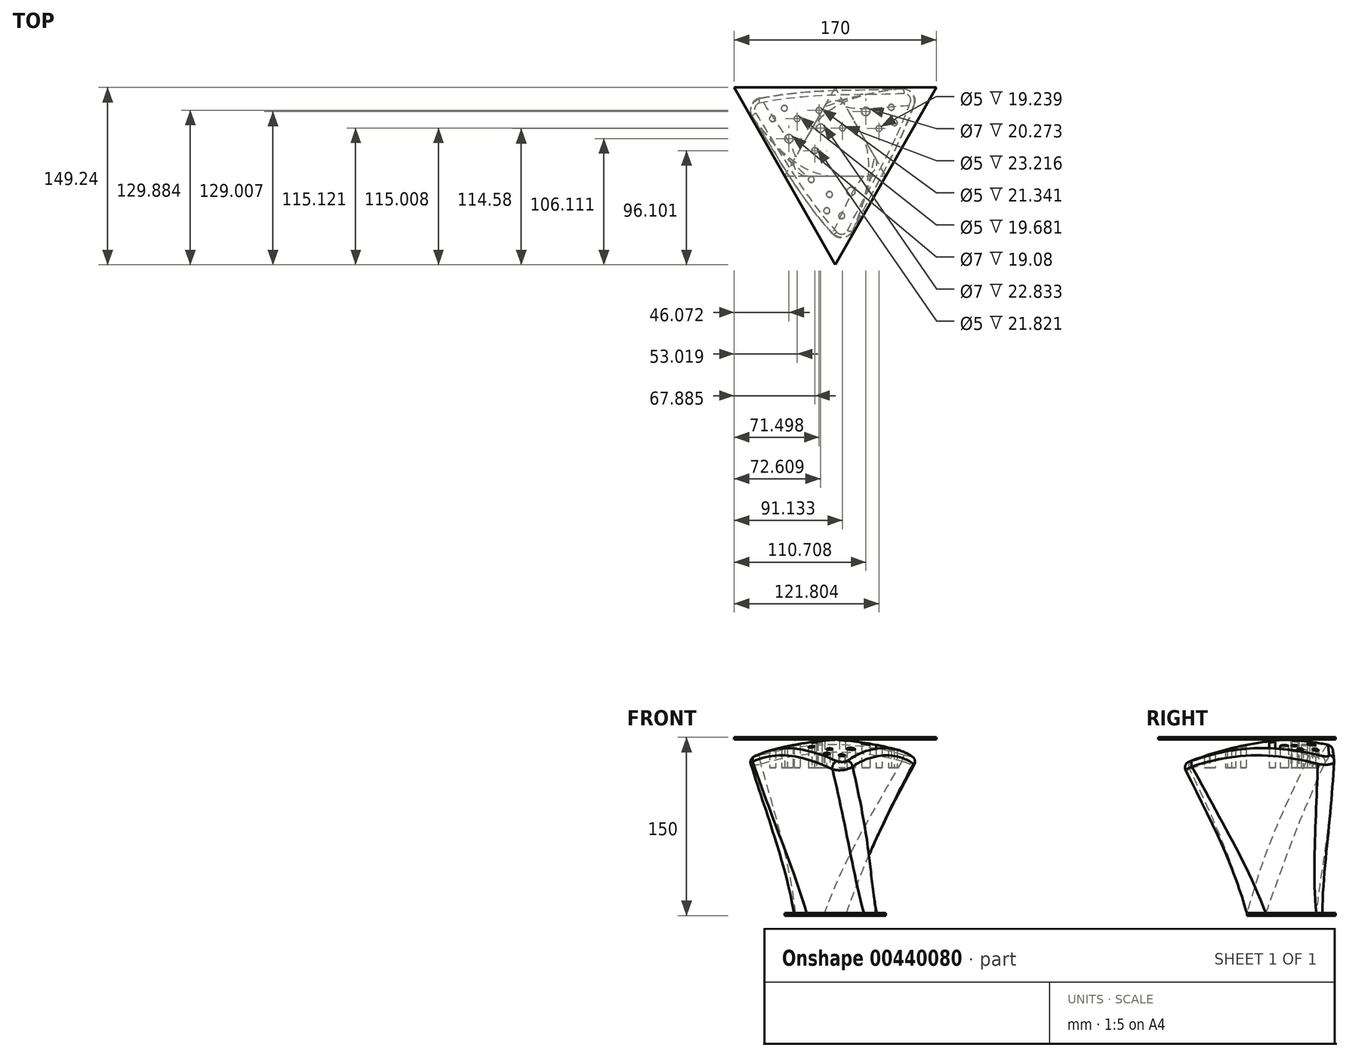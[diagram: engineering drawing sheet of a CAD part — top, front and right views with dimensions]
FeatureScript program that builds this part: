
annotation { "Feature Type Name" : "Feature", "Feature Type Description" : "" }
export const myFeature = defineFeature(function(context is Context, id is Id, definition is map)
    precondition{}
    {
        {
            var Q0;
            Q0=qCreatedBy(makeId("Top.planeOp"),FACE);
            var sketch = newSketch(context, id + "F0", { "sketchPlane" : qUnion([Q0])});
            skLineSegment(sketch, "E0", {"start": v(-85, 50.34) * mm, "end": v(85, 50.34) * mm});
            skLineSegment(sketch, "E1", {"start": v(85, 50.34) * mm, "end": v(0, -98.9) * mm});
            skPoint(sketch, "E1.endSnap0", {"position": v(0, 50.34) * mm});
            skLineSegment(sketch, "E2", {"start": v(0, -98.9) * mm, "end": v(-85, 50.34) * mm});
            skLineSegment(sketch, "E3", {"start": v(0, 50.34) * mm, "end": v(-42.5, -24.28) * mm});
            skLineSegment(sketch, "E4", {"start": v(-42.5, -24.28) * mm, "end": v(42.5, -24.28) * mm});
            skLineSegment(sketch, "E5", {"start": v(42.5, -24.28) * mm, "end": v(0, 50.34) * mm});
            skPoint(sketch, "E6.endSnap0", {"position": v(21.25, 13.03) * mm});
            skSolve(sketch);
        }
        {
            var Q0;
            Q0=makeQuery(id+"F0.imprint","IMPRINT",FACE,{"disambiguationData":[TD([[makeQuery(id+"F0.imprint","IMPRINT",EDGE,{"derivedFrom":sQuery(id+"F0.wireOp",EDGE,"E3")}),1.0]])]});
            extrude(context, id + "F1", {"entities" : qUnion([Q0]), "depth" : 2 * mm});
        }
        {
            var Q0;
            {var subQ3=sQuery(id+"F0.wireOp",EDGE,"E3");Q0=makeQuery(id+"F0.imprint","IMPRINT",FACE,{"disambiguationData":[TD([[makeQuery(id+"F0.imprint","IMPRINT",EDGE,{"derivedFrom":subQ3}),-1.0]])]});}
            var Q1;
            {var subQ3=sQuery(id+"F0.wireOp",EDGE,"E4");Q1=makeQuery(id+"F0.imprint","IMPRINT",FACE,{"disambiguationData":[TD([[makeQuery(id+"F0.imprint","IMPRINT",EDGE,{"derivedFrom":subQ3}),-1.0]])]});}
            var Q2;
            Q2=makeQuery(id+"F0.imprint","IMPRINT",FACE,{"disambiguationData":[TD([[makeQuery(id+"F0.imprint","IMPRINT",EDGE,{"derivedFrom":sQuery(id+"F0.wireOp",EDGE,"E3")}),1.0]])]});
            var Q3;
            {var subQ3=sQuery(id+"F0.wireOp",EDGE,"E5");Q3=makeQuery(id+"F0.imprint","IMPRINT",FACE,{"disambiguationData":[TD([[makeQuery(id+"F0.imprint","IMPRINT",EDGE,{"derivedFrom":subQ3}),-1.0]])]});}
            extrude(context, id + "F2", {"entities" : qUnion([Q0, Q1, Q2, Q3]), "depth" : 2 * mm});
        }
        {
            var Q0;
            Q0=makeQuery(id+"F2.opExtrude","SWEPT_BODY",BODY,{"disambiguationData":[OSD([sQuery(id+"F0.wireOp",EDGE,"E0"),sQuery(id+"F0.wireOp",EDGE,"E1"),sQuery(id+"F0.wireOp",EDGE,"E2")])]});
            transform(context, id + "F3", {"entities" : qUnion([Q0]), "transformType" : TransformType.TRANSLATION_3D, "dx" : 0 * mm, "dy" : 0 * mm, "dz" : 148 * mm, "makeCopy" : false});
        }
        {
            var Q2;
            Q2=makeQuery(id+"F2.opExtrude","CAP_FACE",FACE,{"disambiguationData":[OSD([sQuery(id+"F0.wireOp",EDGE,"E0"),sQuery(id+"F0.wireOp",EDGE,"E1"),sQuery(id+"F0.wireOp",EDGE,"E2")])],"isStart":true});
            var Q3;
            Q3=makeQuery(id+"F1.opExtrude","CAP_FACE",FACE,{"disambiguationData":[OSD([sQuery(id+"F0.wireOp",EDGE,"E3"),sQuery(id+"F0.wireOp",EDGE,"E4"),sQuery(id+"F0.wireOp",EDGE,"E5")])],"isStart":false});
            loft(context, id + "F4", {"sheetProfilesArray" : [{ "sheetProfileEntities" : qUnion([Q2]) }, { "sheetProfileEntities" : qUnion([Q3]) }]});
        }
        {
            var Q0;
            Q0=makeQuery(id+"F4.opLoft","SWEPT_EDGE",EDGE,{"disambiguationData":[OSD([sQuery(id+"F0.wireOp",EDGE,"E0"),sQuery(id+"F0.wireOp",EDGE,"E1"),sQuery(id+"F0.wireOp",EDGE,"E3"),sQuery(id+"F0.wireOp",EDGE,"E5")])]});
            var Q1;
            Q1=makeQuery(id+"F4.opLoft","SWEPT_EDGE",EDGE,{"disambiguationData":[OSD([sQuery(id+"F0.wireOp",EDGE,"E0"),sQuery(id+"F0.wireOp",EDGE,"E2"),sQuery(id+"F0.wireOp",EDGE,"E3"),sQuery(id+"F0.wireOp",EDGE,"E4")])]});
            var Q2;
            Q2=makeQuery(id+"F4.opLoft","SWEPT_EDGE",EDGE,{"disambiguationData":[OSD([sQuery(id+"F0.wireOp",EDGE,"E1"),sQuery(id+"F0.wireOp",EDGE,"E2"),sQuery(id+"F0.wireOp",EDGE,"E4"),sQuery(id+"F0.wireOp",EDGE,"E5")])]});
            fillet(context, id + "F5", {"entities" : qUnion([Q0, Q1, Q2]), "radius" : 10 * mm, "tangentPropagation" : true, "allowEdgeOverflow" : false});
        }
        {
            var Q0;
            Q0=qCreatedBy(makeId("Right.planeOp"),FACE);
            var sketch = newSketch(context, id + "F6", { "sketchPlane" : qUnion([Q0])});
            skLineSegment(sketch, "E7", {"start": v(0, 68.83) * mm, "end": v(131.91, 68.83) * mm});
            skLineSegment(sketch, "E8", {"start": v(131.91, 68.83) * mm, "end": v(131.91, 0) * mm});
            skLineSegment(sketch, "E9", {"start": v(0, 92.79) * mm, "end": v(0, 129.89) * mm});
            skLineSegment(sketch, "E10", {"start": v(0, 68.83) * mm, "end": v(0, 43.97) * mm});
            skArc(sketch, "E11", {"start": v(131.91, 0) * mm, "mid": v(68.82, 30.59) * mm, "end": v(0, 43.97) * mm});
            skSolve(sketch);
        }
        {
            var Q0;
            Q0=makeQuery(id+"F6.imprint","IMPRINT",FACE,{"disambiguationData":[TD([[makeQuery(id+"F6.imprint","IMPRINT",EDGE,{"derivedFrom":sQuery(id+"F6.wireOp",EDGE,"E7")}),-1.0]])]});
            var Q1;
            Q1=sQuery(id+"F6.wireOp",EDGE,"E9");
            revolve(context, id + "F7", {"entities" : qUnion([Q0]), "axis" : qUnion([Q1]), "revolveType" : RevolveType.FULL});
        }
        {
            var Q0;
            Q0=makeQuery(id+"F7.opRevolve","SWEPT_BODY",BODY,{"disambiguationData":[OSD([sQuery(id+"F6.wireOp",EDGE,"pEi6ofau-1SlT-5D8T-A1yP-VA6PnI3HcKg5"),sQuery(id+"F6.wireOp",EDGE,"E7"),sQuery(id+"F6.wireOp",EDGE,"E8"),sQuery(id+"F6.wireOp",EDGE,"E10")])]});
            transform(context, id + "F8", {"entities" : qUnion([Q0]), "transformType" : TransformType.TRANSLATION_3D, "dx" : 0 * mm, "dy" : 10.1 * mm, "dz" : 104 * mm, "makeCopy" : false});
        }
        {
            var Q0;
            Q0=makeQuery(id+"F7.opRevolve","SWEPT_BODY",BODY,{"disambiguationData":[OSD([sQuery(id+"F6.wireOp",EDGE,"E7"),sQuery(id+"F6.wireOp",EDGE,"E8"),sQuery(id+"F6.wireOp",EDGE,"E10"),sQuery(id+"F6.wireOp",EDGE,"E11")])]});
            var Q1;
            Q1=makeQuery(id+"F4.opLoft","SWEPT_BODY",BODY,{"disambiguationData":[OSD([sQuery(id+"F0.wireOp",EDGE,"E0"),sQuery(id+"F0.wireOp",EDGE,"E1"),sQuery(id+"F0.wireOp",EDGE,"E2"),sQuery(id+"F0.wireOp",EDGE,"E3"),sQuery(id+"F0.wireOp",EDGE,"E4"),sQuery(id+"F0.wireOp",EDGE,"E5")])]});
            booleanBodies(context, id + "F9", {"operationType" : BooleanOperationType.SUBTRACTION, "tools" : qUnion([Q0]), "targets" : qUnion([Q1])});
        }
        {
            var Q0;
            {var subQ0=sQuery(id+"F0.wireOp",EDGE,"E2");var subQ1=sQuery(id+"F0.wireOp",EDGE,"E1");var subQ2=sQuery(id+"F0.wireOp",EDGE,"E0");var subQ3=sQuery(id+"F0.wireOp",EDGE,"E4");var subQ4=sQuery(id+"F0.wireOp",EDGE,"E5");var subQ5=sQuery(id+"F0.wireOp",EDGE,"E3");Q0=makeQuery(id+"F9.opBoolean","INTERSECT",EDGE,{"derivedFrom":[makeQuery(id+"F4.opLoft","SWEPT_FACE",FACE,{"disambiguationData":[OSD([subQ2,subQ1,subQ0,subQ5,subQ3,subQ4]),TDD([makeQuery(id+"F1.opExtrude","CAP_VERTEX",VERTEX,{"disambiguationData":[OSD([subQ0,subQ5,subQ3])],"isStart":false}),makeQuery(id+"F1.opExtrude","CAP_VERTEX",VERTEX,{"disambiguationData":[OSD([subQ1,subQ3,subQ4])],"isStart":false}),makeQuery(id+"F1.opExtrude","CAP_EDGE",EDGE,{"disambiguationData":[OSD([subQ3])],"isStart":false}),makeQuery(id+"F2.opExtrude","CAP_VERTEX",VERTEX,{"disambiguationData":[OSD([subQ2,subQ0])],"isStart":true}),makeQuery(id+"F2.opExtrude","CAP_VERTEX",VERTEX,{"disambiguationData":[OSD([subQ1,subQ0])],"isStart":true}),makeQuery(id+"F2.opExtrude","CAP_EDGE",EDGE,{"disambiguationData":[OSD([subQ0])],"isStart":true})])]}),makeQuery(id+"F7.opRevolve","SWEPT_FACE",FACE,{"disambiguationData":[OSD([sQuery(id+"F6.wireOp",EDGE,"E11")])]})]});}
            var Q1;
            Q1=makeQuery(id+"F9.opBoolean","INTERSECT",EDGE,{"derivedFrom":[makeQuery(id+"F5.opFillet","BLEND_FACE",FACE,{"disambiguationData":[OSD([sQuery(id+"F0.wireOp",EDGE,"E1"),sQuery(id+"F0.wireOp",EDGE,"E2"),sQuery(id+"F0.wireOp",EDGE,"E4"),sQuery(id+"F0.wireOp",EDGE,"E5")])]}),makeQuery(id+"F7.opRevolve","SWEPT_FACE",FACE,{"disambiguationData":[OSD([sQuery(id+"F6.wireOp",EDGE,"E11")])]})]});
            var Q2;
            {var subQ0=sQuery(id+"F0.wireOp",EDGE,"E1");var subQ1=sQuery(id+"F0.wireOp",EDGE,"E2");var subQ2=sQuery(id+"F0.wireOp",EDGE,"E0");var subQ3=sQuery(id+"F0.wireOp",EDGE,"E5");var subQ4=sQuery(id+"F0.wireOp",EDGE,"E4");var subQ5=sQuery(id+"F0.wireOp",EDGE,"E3");Q2=makeQuery(id+"F9.opBoolean","INTERSECT",EDGE,{"derivedFrom":[makeQuery(id+"F4.opLoft","SWEPT_FACE",FACE,{"disambiguationData":[OSD([subQ2,subQ0,subQ1,subQ5,subQ4,subQ3]),TDD([makeQuery(id+"F1.opExtrude","CAP_VERTEX",VERTEX,{"disambiguationData":[OSD([subQ2,subQ5,subQ3])],"isStart":false}),makeQuery(id+"F1.opExtrude","CAP_VERTEX",VERTEX,{"disambiguationData":[OSD([subQ0,subQ4,subQ3])],"isStart":false}),makeQuery(id+"F1.opExtrude","CAP_EDGE",EDGE,{"disambiguationData":[OSD([subQ3])],"isStart":false}),makeQuery(id+"F2.opExtrude","CAP_VERTEX",VERTEX,{"disambiguationData":[OSD([subQ2,subQ0])],"isStart":true}),makeQuery(id+"F2.opExtrude","CAP_VERTEX",VERTEX,{"disambiguationData":[OSD([subQ0,subQ1])],"isStart":true}),makeQuery(id+"F2.opExtrude","CAP_EDGE",EDGE,{"disambiguationData":[OSD([subQ0])],"isStart":true})])]}),makeQuery(id+"F7.opRevolve","SWEPT_FACE",FACE,{"disambiguationData":[OSD([sQuery(id+"F6.wireOp",EDGE,"E11")])]})]});}
            var Q3;
            Q3=makeQuery(id+"F9.opBoolean","INTERSECT",EDGE,{"derivedFrom":[makeQuery(id+"F5.opFillet","BLEND_FACE",FACE,{"disambiguationData":[OSD([sQuery(id+"F0.wireOp",EDGE,"E0"),sQuery(id+"F0.wireOp",EDGE,"E1"),sQuery(id+"F0.wireOp",EDGE,"E3"),sQuery(id+"F0.wireOp",EDGE,"E5")])]}),makeQuery(id+"F7.opRevolve","SWEPT_FACE",FACE,{"disambiguationData":[OSD([sQuery(id+"F6.wireOp",EDGE,"E11")])]})]});
            var Q4;
            {var subQ0=sQuery(id+"F0.wireOp",EDGE,"E0");var subQ1=sQuery(id+"F0.wireOp",EDGE,"E1");var subQ2=sQuery(id+"F0.wireOp",EDGE,"E2");var subQ3=sQuery(id+"F0.wireOp",EDGE,"E3");var subQ4=sQuery(id+"F0.wireOp",EDGE,"E4");var subQ5=sQuery(id+"F0.wireOp",EDGE,"E5");Q4=makeQuery(id+"F9.opBoolean","INTERSECT",EDGE,{"derivedFrom":[makeQuery(id+"F4.opLoft","SWEPT_FACE",FACE,{"disambiguationData":[OSD([subQ0,subQ1,subQ2,subQ3,subQ4,subQ5]),TDD([makeQuery(id+"F1.opExtrude","CAP_VERTEX",VERTEX,{"disambiguationData":[OSD([subQ0,subQ3,subQ5])],"isStart":false}),makeQuery(id+"F1.opExtrude","CAP_VERTEX",VERTEX,{"disambiguationData":[OSD([subQ2,subQ3,subQ4])],"isStart":false}),makeQuery(id+"F1.opExtrude","CAP_EDGE",EDGE,{"disambiguationData":[OSD([subQ3])],"isStart":false}),makeQuery(id+"F2.opExtrude","CAP_VERTEX",VERTEX,{"disambiguationData":[OSD([subQ0,subQ2])],"isStart":true}),makeQuery(id+"F2.opExtrude","CAP_VERTEX",VERTEX,{"disambiguationData":[OSD([subQ0,subQ1])],"isStart":true}),makeQuery(id+"F2.opExtrude","CAP_EDGE",EDGE,{"disambiguationData":[OSD([subQ0])],"isStart":true})])]}),makeQuery(id+"F7.opRevolve","SWEPT_FACE",FACE,{"disambiguationData":[OSD([sQuery(id+"F6.wireOp",EDGE,"E11")])]})]});}
            var Q5;
            Q5=makeQuery(id+"F9.opBoolean","INTERSECT",EDGE,{"derivedFrom":[makeQuery(id+"F5.opFillet","BLEND_FACE",FACE,{"disambiguationData":[OSD([sQuery(id+"F0.wireOp",EDGE,"E0"),sQuery(id+"F0.wireOp",EDGE,"E2"),sQuery(id+"F0.wireOp",EDGE,"E3"),sQuery(id+"F0.wireOp",EDGE,"E4")])]}),makeQuery(id+"F7.opRevolve","SWEPT_FACE",FACE,{"disambiguationData":[OSD([sQuery(id+"F6.wireOp",EDGE,"E11")])]})]});
            fillet(context, id + "F10", {"entities" : qUnion([Q0, Q1, Q2, Q3, Q4, Q5]), "radius" : 5 * mm, "tangentPropagation" : true, "allowEdgeOverflow" : false});
        }
        {
            var Q0;
            Q0=qCreatedBy(makeId("Top.planeOp"),FACE);
            var sketch = newSketch(context, id + "F11", { "sketchPlane" : qUnion([Q0])});
            skCircle(sketch, "E12", {"center": v(0, 0) * mm, "radius": 2 * mm});
            skCircle(sketch, "E13", {"center": v(-17.11, -2.8) * mm, "radius": 2.5 * mm});
            skCircle(sketch, "E14", {"center": v(-12.4, 16.1) * mm, "radius": 3.5 * mm});
            skCircle(sketch, "E15", {"center": v(-38.93, 7.21) * mm, "radius": 3.5 * mm});
            skCircle(sketch, "E16", {"center": v(-31.98, 24.03) * mm, "radius": 2.5 * mm});
            skCircle(sketch, "E17", {"center": v(-52.68, 24.03) * mm, "radius": 2.5 * mm});
            skCircle(sketch, "E18", {"center": v(-42.68, 32.8) * mm, "radius": 2.5 * mm});
            skCircle(sketch, "E19", {"center": v(-13.5, 30.98) * mm, "radius": 2.5 * mm});
            skCircle(sketch, "E20.1.0", {"center": v(5.53, -57.64) * mm, "radius": 2.5 * mm});
            skCircle(sketch, "E20.1.1", {"center": v(-7.06, -53.36) * mm, "radius": 2.5 * mm});
            skCircle(sketch, "E20.1.2", {"center": v(-4.82, -39.71) * mm, "radius": 2.5 * mm});
            skCircle(sketch, "E20.1.3", {"center": v(13.22, -37.32) * mm, "radius": 3.5 * mm});
            skCircle(sketch, "E20.1.4", {"center": v(10.98, -13.42) * mm, "radius": 2.5 * mm});
            skCircle(sketch, "E20.1.5", {"center": v(-7.75, -18.78) * mm, "radius": 3.5 * mm});
            skCircle(sketch, "E20.1.6", {"center": v(-20.08, -27.19) * mm, "radius": 2.5 * mm});
            skCircle(sketch, "E20.2.0", {"center": v(47.15, 33.6) * mm, "radius": 2.5 * mm});
            skCircle(sketch, "E20.2.1", {"center": v(49.74, 20.57) * mm, "radius": 2.5 * mm});
            skCircle(sketch, "E20.2.2", {"center": v(36.8, 15.68) * mm, "radius": 2.5 * mm});
            skCircle(sketch, "E20.2.3", {"center": v(25.7, 30.1) * mm, "radius": 3.5 * mm});
            skCircle(sketch, "E20.2.4", {"center": v(6.13, 16.22) * mm, "radius": 2.5 * mm});
            skCircle(sketch, "E20.2.5", {"center": v(20.15, 2.68) * mm, "radius": 3.5 * mm});
            skCircle(sketch, "E20.2.6", {"center": v(33.58, -3.8) * mm, "radius": 2.5 * mm});
            skSolve(sketch);
        }
        {
            var Q0;
            Q0 = qSketchRegion(id + "F11", true);
            extrude(context, id + "F12", {"entities" : qUnion([Q0]), "depth" : 25 * mm});
        }
        {
            var Q0;
            Q0=makeQuery(id+"F12.opExtrude","SWEPT_BODY",BODY,{"disambiguationData":[OSD([sQuery(id+"F11.wireOp",EDGE,"E12")])]});
            var Q1;
            Q1=makeQuery(id+"F12.opExtrude","SWEPT_BODY",BODY,{"disambiguationData":[OSD([sQuery(id+"F11.wireOp",EDGE,"E13")])]});
            var Q2;
            Q2=makeQuery(id+"F12.opExtrude","SWEPT_BODY",BODY,{"disambiguationData":[OSD([sQuery(id+"F11.wireOp",EDGE,"E14")])]});
            var Q3;
            Q3=makeQuery(id+"F12.opExtrude","SWEPT_BODY",BODY,{"disambiguationData":[OSD([sQuery(id+"F11.wireOp",EDGE,"E15")])]});
            var Q4;
            Q4=makeQuery(id+"F12.opExtrude","SWEPT_BODY",BODY,{"disambiguationData":[OSD([sQuery(id+"F11.wireOp",EDGE,"E16")])]});
            var Q5;
            Q5=makeQuery(id+"F12.opExtrude","SWEPT_BODY",BODY,{"disambiguationData":[OSD([sQuery(id+"F11.wireOp",EDGE,"E17")])]});
            var Q6;
            Q6=makeQuery(id+"F12.opExtrude","SWEPT_BODY",BODY,{"disambiguationData":[OSD([sQuery(id+"F11.wireOp",EDGE,"E18")])]});
            var Q7;
            Q7=makeQuery(id+"F12.opExtrude","SWEPT_BODY",BODY,{"disambiguationData":[OSD([sQuery(id+"F11.wireOp",EDGE,"E19")])]});
            var Q8;
            Q8=makeQuery(id+"F12.opExtrude","SWEPT_BODY",BODY,{"disambiguationData":[OSD([sQuery(id+"F11.wireOp",EDGE,"E20.1.0")])]});
            var Q9;
            Q9=makeQuery(id+"F12.opExtrude","SWEPT_BODY",BODY,{"disambiguationData":[OSD([sQuery(id+"F11.wireOp",EDGE,"E20.1.1")])]});
            var Q10;
            Q10=makeQuery(id+"F12.opExtrude","SWEPT_BODY",BODY,{"disambiguationData":[OSD([sQuery(id+"F11.wireOp",EDGE,"E20.1.2")])]});
            var Q11;
            Q11=makeQuery(id+"F12.opExtrude","SWEPT_BODY",BODY,{"disambiguationData":[OSD([sQuery(id+"F11.wireOp",EDGE,"E20.1.3")])]});
            var Q12;
            Q12=makeQuery(id+"F12.opExtrude","SWEPT_BODY",BODY,{"disambiguationData":[OSD([sQuery(id+"F11.wireOp",EDGE,"E20.1.4")])]});
            var Q13;
            Q13=makeQuery(id+"F12.opExtrude","SWEPT_BODY",BODY,{"disambiguationData":[OSD([sQuery(id+"F11.wireOp",EDGE,"E20.1.5")])]});
            var Q14;
            Q14=makeQuery(id+"F12.opExtrude","SWEPT_BODY",BODY,{"disambiguationData":[OSD([sQuery(id+"F11.wireOp",EDGE,"E20.1.6")])]});
            var Q15;
            Q15=makeQuery(id+"F12.opExtrude","SWEPT_BODY",BODY,{"disambiguationData":[OSD([sQuery(id+"F11.wireOp",EDGE,"E20.2.0")])]});
            var Q16;
            Q16=makeQuery(id+"F12.opExtrude","SWEPT_BODY",BODY,{"disambiguationData":[OSD([sQuery(id+"F11.wireOp",EDGE,"E20.2.1")])]});
            var Q17;
            Q17=makeQuery(id+"F12.opExtrude","SWEPT_BODY",BODY,{"disambiguationData":[OSD([sQuery(id+"F11.wireOp",EDGE,"E20.2.2")])]});
            var Q18;
            Q18=makeQuery(id+"F12.opExtrude","SWEPT_BODY",BODY,{"disambiguationData":[OSD([sQuery(id+"F11.wireOp",EDGE,"E20.2.3")])]});
            var Q19;
            Q19=makeQuery(id+"F12.opExtrude","SWEPT_BODY",BODY,{"disambiguationData":[OSD([sQuery(id+"F11.wireOp",EDGE,"E20.2.4")])]});
            var Q20;
            Q20=makeQuery(id+"F12.opExtrude","SWEPT_BODY",BODY,{"disambiguationData":[OSD([sQuery(id+"F11.wireOp",EDGE,"E20.2.5")])]});
            var Q21;
            Q21=makeQuery(id+"F12.opExtrude","SWEPT_BODY",BODY,{"disambiguationData":[OSD([sQuery(id+"F11.wireOp",EDGE,"E20.2.6")])]});
            transform(context, id + "F13", {"entities" : qUnion([Q0, Q1, Q2, Q3, Q4, Q5, Q6, Q7, Q8, Q9, Q10, Q11, Q12, Q13, Q14, Q15, Q16, Q17, Q18, Q19, Q20, Q21]), "transformType" : TransformType.TRANSLATION_3D, "dx" : 0 * mm, "dy" : 0 * mm, "dz" : 124.3 * mm, "makeCopy" : false});
        }
        {
            var Q0;
            Q0=makeQuery(id+"F12.opExtrude","SWEPT_BODY",BODY,{"disambiguationData":[OSD([sQuery(id+"F11.wireOp",EDGE,"E12")])]});
            var Q1;
            Q1=makeQuery(id+"F12.opExtrude","SWEPT_BODY",BODY,{"disambiguationData":[OSD([sQuery(id+"F11.wireOp",EDGE,"E13")])]});
            var Q2;
            Q2=makeQuery(id+"F12.opExtrude","SWEPT_BODY",BODY,{"disambiguationData":[OSD([sQuery(id+"F11.wireOp",EDGE,"E14")])]});
            var Q3;
            Q3=makeQuery(id+"F12.opExtrude","SWEPT_BODY",BODY,{"disambiguationData":[OSD([sQuery(id+"F11.wireOp",EDGE,"E15")])]});
            var Q4;
            Q4=makeQuery(id+"F12.opExtrude","SWEPT_BODY",BODY,{"disambiguationData":[OSD([sQuery(id+"F11.wireOp",EDGE,"E16")])]});
            var Q5;
            Q5=makeQuery(id+"F12.opExtrude","SWEPT_BODY",BODY,{"disambiguationData":[OSD([sQuery(id+"F11.wireOp",EDGE,"E17")])]});
            var Q6;
            Q6=makeQuery(id+"F12.opExtrude","SWEPT_BODY",BODY,{"disambiguationData":[OSD([sQuery(id+"F11.wireOp",EDGE,"E18")])]});
            var Q7;
            Q7=makeQuery(id+"F12.opExtrude","SWEPT_BODY",BODY,{"disambiguationData":[OSD([sQuery(id+"F11.wireOp",EDGE,"E19")])]});
            var Q8;
            Q8=makeQuery(id+"F12.opExtrude","SWEPT_BODY",BODY,{"disambiguationData":[OSD([sQuery(id+"F11.wireOp",EDGE,"E20.1.0")])]});
            var Q9;
            Q9=makeQuery(id+"F12.opExtrude","SWEPT_BODY",BODY,{"disambiguationData":[OSD([sQuery(id+"F11.wireOp",EDGE,"E20.1.1")])]});
            var Q10;
            Q10=makeQuery(id+"F12.opExtrude","SWEPT_BODY",BODY,{"disambiguationData":[OSD([sQuery(id+"F11.wireOp",EDGE,"E20.1.2")])]});
            var Q11;
            Q11=makeQuery(id+"F12.opExtrude","SWEPT_BODY",BODY,{"disambiguationData":[OSD([sQuery(id+"F11.wireOp",EDGE,"E20.1.3")])]});
            var Q12;
            Q12=makeQuery(id+"F12.opExtrude","SWEPT_BODY",BODY,{"disambiguationData":[OSD([sQuery(id+"F11.wireOp",EDGE,"E20.1.4")])]});
            var Q13;
            Q13=makeQuery(id+"F12.opExtrude","SWEPT_BODY",BODY,{"disambiguationData":[OSD([sQuery(id+"F11.wireOp",EDGE,"E20.1.5")])]});
            var Q14;
            Q14=makeQuery(id+"F12.opExtrude","SWEPT_BODY",BODY,{"disambiguationData":[OSD([sQuery(id+"F11.wireOp",EDGE,"E20.1.6")])]});
            var Q15;
            Q15=makeQuery(id+"F12.opExtrude","SWEPT_BODY",BODY,{"disambiguationData":[OSD([sQuery(id+"F11.wireOp",EDGE,"E20.2.0")])]});
            var Q16;
            Q16=makeQuery(id+"F12.opExtrude","SWEPT_BODY",BODY,{"disambiguationData":[OSD([sQuery(id+"F11.wireOp",EDGE,"E20.2.1")])]});
            var Q17;
            Q17=makeQuery(id+"F12.opExtrude","SWEPT_BODY",BODY,{"disambiguationData":[OSD([sQuery(id+"F11.wireOp",EDGE,"E20.2.2")])]});
            var Q18;
            Q18=makeQuery(id+"F12.opExtrude","SWEPT_BODY",BODY,{"disambiguationData":[OSD([sQuery(id+"F11.wireOp",EDGE,"E20.2.3")])]});
            var Q19;
            Q19=makeQuery(id+"F12.opExtrude","SWEPT_BODY",BODY,{"disambiguationData":[OSD([sQuery(id+"F11.wireOp",EDGE,"E20.2.4")])]});
            var Q20;
            Q20=makeQuery(id+"F12.opExtrude","SWEPT_BODY",BODY,{"disambiguationData":[OSD([sQuery(id+"F11.wireOp",EDGE,"E20.2.5")])]});
            var Q21;
            Q21=makeQuery(id+"F12.opExtrude","SWEPT_BODY",BODY,{"disambiguationData":[OSD([sQuery(id+"F11.wireOp",EDGE,"E20.2.6")])]});
            var Q22;
            Q22=makeQuery(id+"F4.opLoft","SWEPT_BODY",BODY,{"disambiguationData":[OSD([sQuery(id+"F0.wireOp",EDGE,"E0"),sQuery(id+"F0.wireOp",EDGE,"E1"),sQuery(id+"F0.wireOp",EDGE,"E2"),sQuery(id+"F0.wireOp",EDGE,"E3"),sQuery(id+"F0.wireOp",EDGE,"E4"),sQuery(id+"F0.wireOp",EDGE,"E5")])]});
            booleanBodies(context, id + "F14", {"operationType" : BooleanOperationType.SUBTRACTION, "tools" : qUnion([Q0, Q1, Q2, Q3, Q4, Q5, Q6, Q7, Q8, Q9, Q10, Q11, Q12, Q13, Q14, Q15, Q16, Q17, Q18, Q19, Q20, Q21]), "targets" : qUnion([Q22])});
        }
    });
